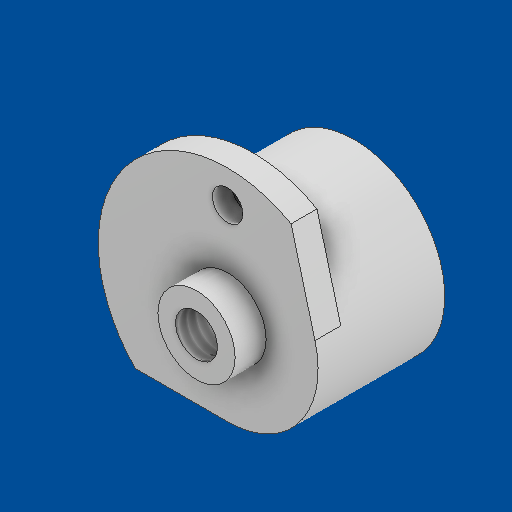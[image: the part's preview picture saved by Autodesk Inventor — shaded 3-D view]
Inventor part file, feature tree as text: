
AUTODESK INVENTOR PART (.ipt)
format: ipt  version: 2025 (Build 290162000, 162)  size: 149,504 bytes
history: native  units: in
note: dims shown in document units (in); Inventor stores cm internally (conversion verified against a paired STEP export)
features: direct_edit x1, hole x1, sketch x1, other x1
ambient origin geometry x8: Origin, YZ Plane, XZ Plane, XY Plane, X Axis, Y Axis, Z Axis, Center Point
bodies: Solid1 (feature_tree), Body1 (feature_tree)
feature tree (4):
  direct_edit  "Direct Edit1"
  hole  "Hole1"  [1 undecoded]
  sketch  "Sketch1"  dims[d0=0.0394in d1=0.0787in d2=0.1276in d3=0.3937in d4=0.1575in d5=0.0787in d6=90.0deg d7=0.315in d8=0.8108in]
  other  "Size1"
note: 1 required parameter value undecoded (feature->parameter linkage not recoverable at this tier; creation-order binding heuristic only, values carry confidence <= 0.55)
